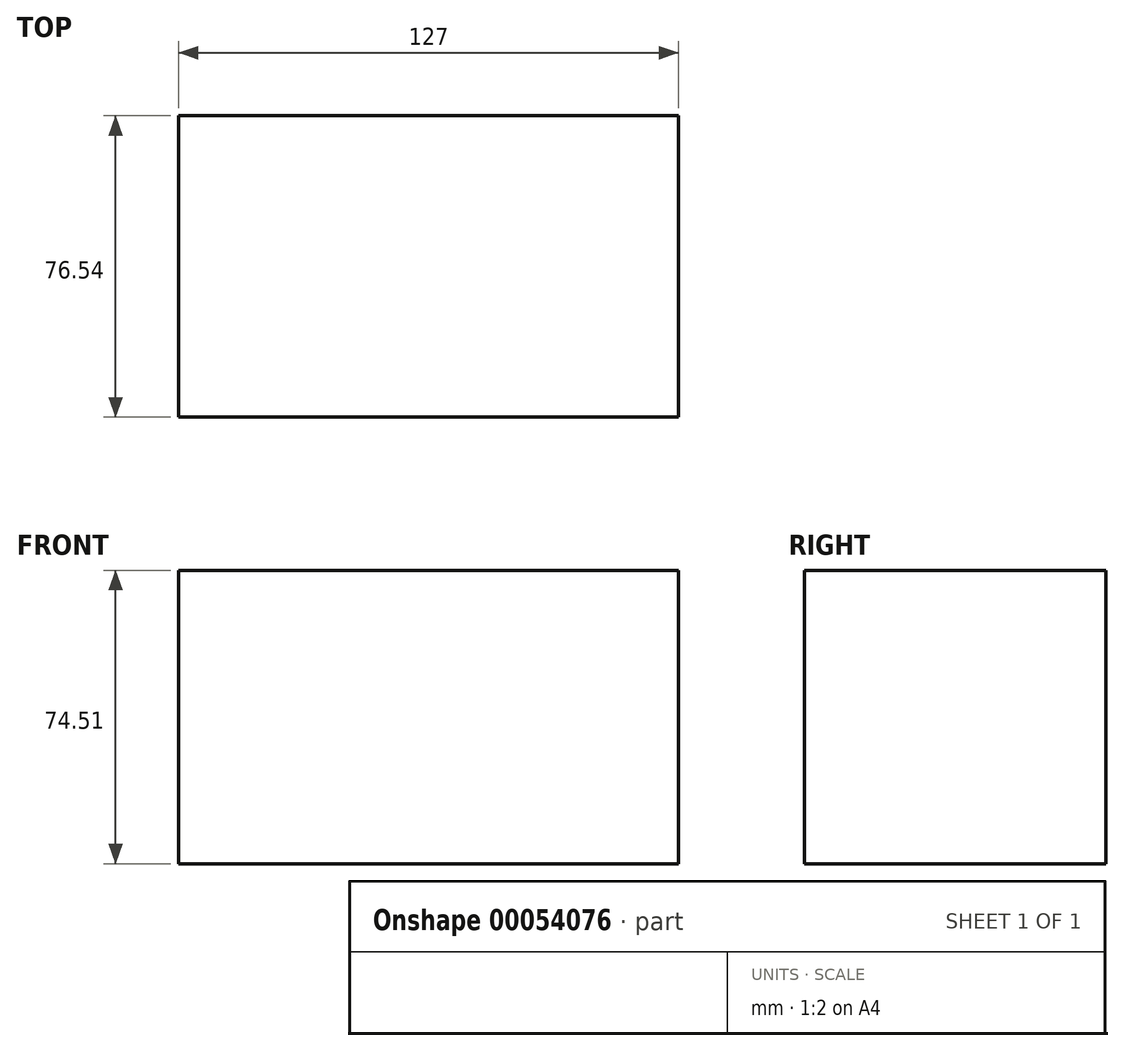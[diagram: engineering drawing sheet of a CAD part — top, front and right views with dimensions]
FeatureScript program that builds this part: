
annotation { "Feature Type Name" : "Feature", "Feature Type Description" : "" }
export const myFeature = defineFeature(function(context is Context, id is Id, definition is map)
    precondition{}
    {
        {
            var Q0;
            Q0=qCreatedBy(makeId("Right.planeOp"),FACE);
            var sketch = newSketch(context, id + "F0", { "sketchPlane" : qUnion([Q0])});
            skLineSegment(sketch, "E0", {"start": v(0, 74.5) * mm, "end": v(76.54, 74.5) * mm});
            skLineSegment(sketch, "E1", {"start": v(76.54, 74.5) * mm, "end": v(76.54, 0) * mm});
            skLineSegment(sketch, "E2", {"start": v(0, 0) * mm, "end": v(76.54, 0) * mm});
            skLineSegment(sketch, "E3", {"start": v(0, 74.5) * mm, "end": v(0, 0) * mm});
            skSolve(sketch);
        }
        {
            var Q0;
            Q0=makeQuery(id+"F0.imprint","IMPRINT",FACE,{"disambiguationData":[TD([[makeQuery(id+"F0.imprint","IMPRINT",EDGE,{"derivedFrom":sQuery(id+"F0.wireOp",EDGE,"E0")}),-1.0]])]});
            extrude(context, id + "F1", {"entities" : qUnion([Q0]), "depth" : 127 * mm});
        }
        {
            var Q0;
            Q0=makeQuery(id+"F1.opExtrude","SWEPT_FACE",FACE,{"disambiguationData":[OSD([sQuery(id+"F0.wireOp",EDGE,"E0")])]});
            var sketch = newSketch(context, id + "F2", { "sketchPlane" : qUnion([Q0])});
            skSolve(sketch);
        }
        {
            var Q0;
            {var subQ0=sQuery(id+"F0.wireOp",EDGE,"E0");Q0=makeQuery(id+"F2.imprint","IMPRINT",FACE,{"disambiguationData":[TD([[makeQuery(id+"F2.imprint","IMPRINT",EDGE,{"derivedFrom":makeQuery(id+"F1.opExtrude","CAP_EDGE",EDGE,{"disambiguationData":[OSD([subQ0])],"isStart":true})}),-1.0]])]});}
            var sketch = newSketch(context, id + "F3", { "sketchPlane" : qUnion([Q0])});
            skLineSegment(sketch, "E4", {"start": v(126.08, 75.67) * mm, "end": v(2.25, 0) * mm, "construction": true});
            skCircle(sketch, "E5", {"center": v(69.9, 41.34) * mm, "radius": 24.43 * mm});
            skSolve(sketch);
        }
        {
            var Q0;
            Q0 = qSketchRegion(id + "F3", true);
            var Q1;
            Q1=sQuery(id+"F3.wireOp",EDGE,"E5");
            extrude(context, id + "F4", {"entities" : qUnion([Q0]), "operationType" : NewBodyOperationType.REMOVE, "surfaceEntities" : qUnion([Q1]), "depth" : 25.4 * mm});
        }
    });
